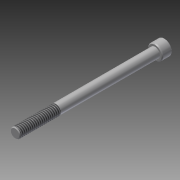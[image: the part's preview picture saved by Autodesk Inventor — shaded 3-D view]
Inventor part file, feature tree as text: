
AUTODESK INVENTOR PART (.ipt)
format: ipt  version: 2013 (Build 170138000, 138)  size: 97,280 bytes
history: native  units: in
note: dims shown in document units (in); Inventor stores cm internally (conversion verified against a paired STEP export)
features: extrude x3, sketch x3, chamfer x1, thread x1
ambient origin geometry x8: Origin, YZ Plane, XZ Plane, XY Plane, X Axis, Y Axis, Z Axis, Center Point
bodies: Solid1 (feature_tree)
feature tree (8):
  extrude  "Extrusion1"  Depth=3.5in TaperAngle=0.0deg
  extrude  "Extrusion2"  Depth=0.25in TaperAngle=0.0deg
  extrude  "Extrusion3"  Depth=0.125in TaperAngle=0.0deg
  chamfer  "Chamfer1"  Distance=0.02in Angle=45.0deg
  thread  "Thread1"  [1 undecoded]
  sketch  "Sketch1"  dims[d0=0.25in d1=3.5in d2=0.0in]
  sketch  "Sketch2"  dims[d3=0.375in d4=0.25in d5=0.0in]
  sketch  "Sketch3"  dims[d6=0.1875in d7=0.125in d8=0.0in d9=0.02in d10=0.125in d11=45.0deg d12=1.0in d13=0.0in]
note: 1 required parameter value undecoded (feature->parameter linkage not recoverable at this tier; creation-order binding heuristic only, values carry confidence <= 0.55)
